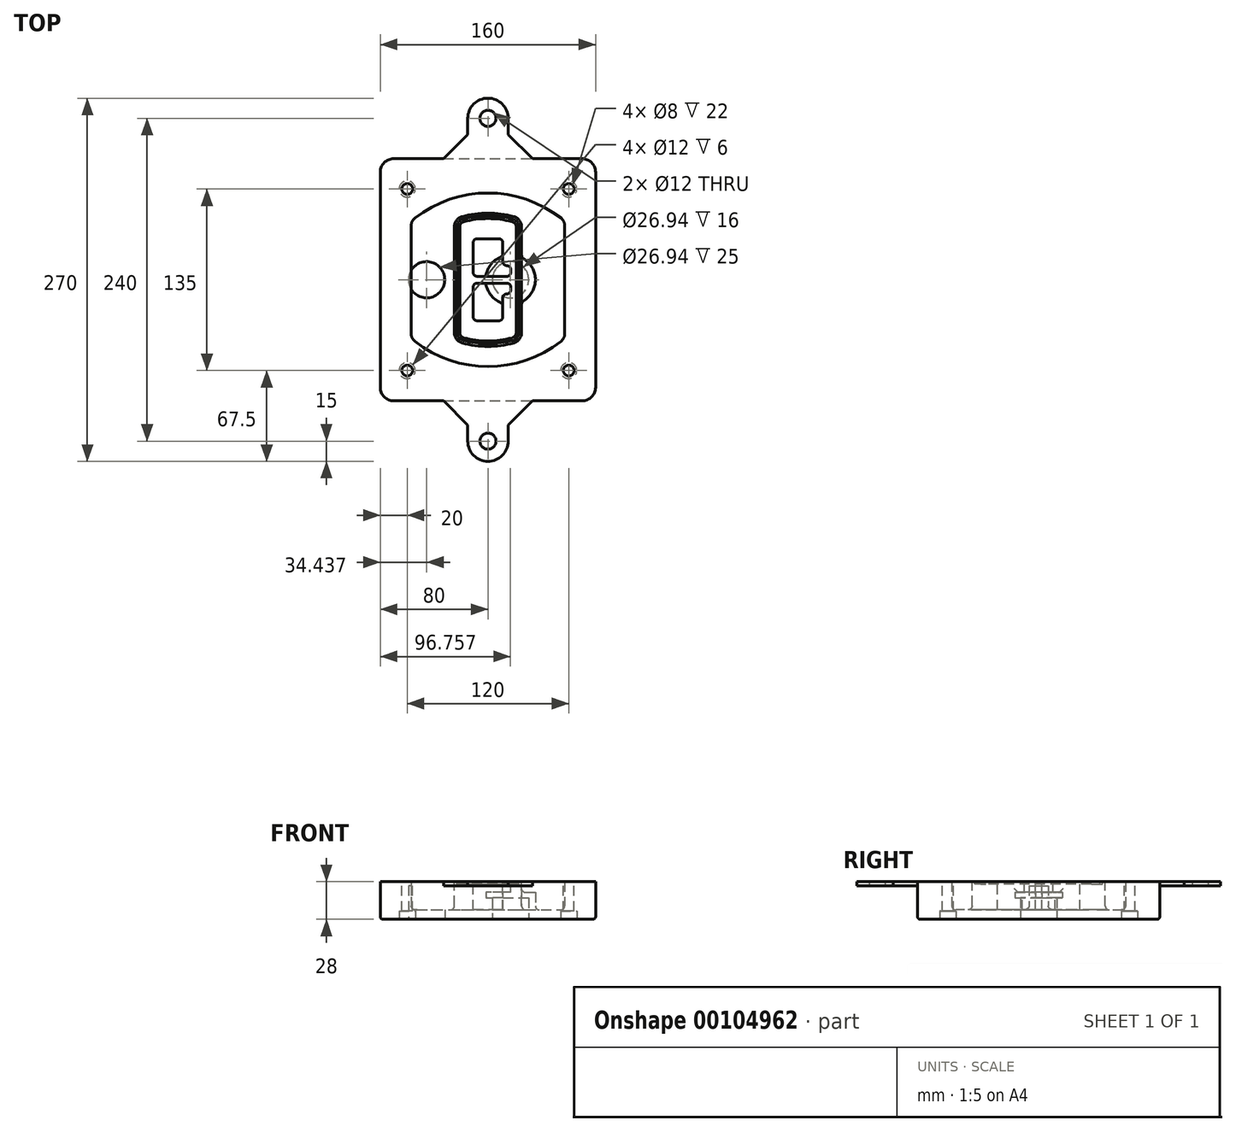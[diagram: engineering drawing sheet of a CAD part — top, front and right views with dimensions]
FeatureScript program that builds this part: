
annotation { "Feature Type Name" : "Feature", "Feature Type Description" : "" }
export const myFeature = defineFeature(function(context is Context, id is Id, definition is map)
    precondition{}
    {
        {
            var Q0;
            Q0=qCreatedBy(makeId("Top.planeOp"),FACE);
            var sketch = newSketch(context, id + "F0", { "sketchPlane" : qUnion([Q0])});
            skPoint(sketch, "E0.rect.middle", {"position": v(0, 0) * mm});
            skLineSegment(sketch, "E1.bottom", {"start": v(-70, -90) * mm, "end": v(70, -90) * mm});
            skLineSegment(sketch, "E1.top", {"start": v(-70, 90) * mm, "end": v(70, 90) * mm});
            skLineSegment(sketch, "E1.left", {"start": v(-80, -80) * mm, "end": v(-80, 80) * mm});
            skLineSegment(sketch, "E1.right", {"start": v(80, -80) * mm, "end": v(80, 80) * mm});
            skLineSegment(sketch, "E2", {"start": v(-80, 90) * mm, "end": v(80, -90) * mm, "construction": true});
            skLineSegment(sketch, "E3", {"start": v(80, 90) * mm, "end": v(-80, -90) * mm, "construction": true});
            skCircle(sketch, "E4", {"center": v(-60, 67.5) * mm, "radius": 4 * mm});
            skCircle(sketch, "E5", {"center": v(60, 67.5) * mm, "radius": 4 * mm});
            skCircle(sketch, "E6", {"center": v(60, -67.5) * mm, "radius": 4 * mm});
            skCircle(sketch, "E7", {"center": v(-60, -67.5) * mm, "radius": 4 * mm});
            skLineSegment(sketch, "E8", {"start": v(-60, 67.5) * mm, "end": v(60, 67.5) * mm, "construction": true});
            skLineSegment(sketch, "E9", {"start": v(60, 67.5) * mm, "end": v(60, -67.5) * mm, "construction": true});
            skLineSegment(sketch, "E10", {"start": v(60, -67.5) * mm, "end": v(-60, -67.5) * mm, "construction": true});
            skLineSegment(sketch, "E11", {"start": v(-60, -67.5) * mm, "end": v(-60, 67.5) * mm, "construction": true});
            skLineSegment(sketch, "E12", {"start": v(-60, 40.3) * mm, "end": v(-60, -40.3) * mm});
            skLineSegment(sketch, "E13", {"start": v(60, 40.3) * mm, "end": v(60, -40.3) * mm});
            skArc(sketch, "E14", {"start": v(56.15, 48.18) * mm, "mid": v(0, 67.5) * mm, "end": v(-56.15, 48.18) * mm});
            skArc(sketch, "E15", {"start": v(-56.15, -48.18) * mm, "mid": v(0, -67.5) * mm, "end": v(56.15, -48.18) * mm});
            skLineSegment(sketch, "E16", {"start": v(-60, 0) * mm, "end": v(60, 0) * mm, "construction": true});
            skPoint(sketch, "E17.visualSharp", {"position": v(-60, -45) * mm});
            skArc(sketch, "E17.filletArc", {"start": v(-60, -40.3) * mm, "mid": v(-58.99, -44.68) * mm, "end": v(-56.15, -48.18) * mm});
            skPoint(sketch, "E18.visualSharp", {"position": v(-60, 45) * mm});
            skArc(sketch, "E18.filletArc", {"start": v(-56.15, 48.18) * mm, "mid": v(-58.99, 44.68) * mm, "end": v(-60, 40.3) * mm});
            skPoint(sketch, "E19.visualSharp", {"position": v(60, 45) * mm});
            skArc(sketch, "E19.filletArc", {"start": v(60, 40.3) * mm, "mid": v(58.99, 44.68) * mm, "end": v(56.15, 48.18) * mm});
            skPoint(sketch, "E20.visualSharp", {"position": v(60, -45) * mm});
            skArc(sketch, "E20.filletArc", {"start": v(56.15, -48.18) * mm, "mid": v(58.99, -44.68) * mm, "end": v(60, -40.3) * mm});
            skPoint(sketch, "E21.visualSharp", {"position": v(-80, 90) * mm});
            skArc(sketch, "E21.filletArc", {"start": v(-70, 90) * mm, "mid": v(-77.07, 87.07) * mm, "end": v(-80, 80) * mm});
            skPoint(sketch, "E22.visualSharp", {"position": v(80, 90) * mm});
            skArc(sketch, "E22.filletArc", {"start": v(80, 80) * mm, "mid": v(77.07, 87.07) * mm, "end": v(70, 90) * mm});
            skPoint(sketch, "E23.visualSharp", {"position": v(80, -90) * mm});
            skArc(sketch, "E23.filletArc", {"start": v(70, -90) * mm, "mid": v(77.07, -87.07) * mm, "end": v(80, -80) * mm});
            skPoint(sketch, "E24.visualSharp", {"position": v(-80, -90) * mm});
            skArc(sketch, "E24.filletArc", {"start": v(-80, -80) * mm, "mid": v(-77.07, -87.07) * mm, "end": v(-70, -90) * mm});
            skArc(sketch, "E25.0", {"start": v(57, 40.3) * mm, "mid": v(56.3, 43.36) * mm, "end": v(54.3, 45.81) * mm});
            skLineSegment(sketch, "E25.1", {"start": v(57, 40.3) * mm, "end": v(57, -40.3) * mm});
            skArc(sketch, "E25.2", {"start": v(54.3, -45.81) * mm, "mid": v(56.3, -43.36) * mm, "end": v(57, -40.3) * mm});
            skArc(sketch, "E25.3", {"start": v(-54.3, -45.81) * mm, "mid": v(0, -64.5) * mm, "end": v(54.3, -45.81) * mm});
            skArc(sketch, "E25.4", {"start": v(-57, -40.3) * mm, "mid": v(-56.3, -43.36) * mm, "end": v(-54.3, -45.81) * mm});
            skArc(sketch, "E25.5", {"start": v(54.3, 45.81) * mm, "mid": v(0, 64.5) * mm, "end": v(-54.3, 45.81) * mm});
            skLineSegment(sketch, "E25.6", {"start": v(-57, 40.3) * mm, "end": v(-57, -40.3) * mm});
            skArc(sketch, "E25.7", {"start": v(-54.3, 45.81) * mm, "mid": v(-56.3, 43.36) * mm, "end": v(-57, 40.3) * mm});
            skArc(sketch, "E26.0", {"start": v(-58.62, 51.33) * mm, "mid": v(-62.58, 46.43) * mm, "end": v(-64, 40.3) * mm});
            skArc(sketch, "E26.1", {"start": v(58.62, 51.33) * mm, "mid": v(0, 71.5) * mm, "end": v(-58.62, 51.33) * mm});
            skArc(sketch, "E26.2", {"start": v(64, 40.3) * mm, "mid": v(62.58, 46.43) * mm, "end": v(58.62, 51.33) * mm});
            skLineSegment(sketch, "E26.3", {"start": v(64, 40.3) * mm, "end": v(64, -40.3) * mm});
            skArc(sketch, "E26.4", {"start": v(58.62, -51.33) * mm, "mid": v(62.58, -46.43) * mm, "end": v(64, -40.3) * mm});
            skLineSegment(sketch, "E26.5", {"start": v(-64, 40.3) * mm, "end": v(-64, -40.3) * mm});
            skArc(sketch, "E26.6", {"start": v(-58.62, -51.33) * mm, "mid": v(0, -71.5) * mm, "end": v(58.62, -51.33) * mm});
            skArc(sketch, "E26.7", {"start": v(-64, -40.3) * mm, "mid": v(-62.58, -46.43) * mm, "end": v(-58.62, -51.33) * mm});
            skSolve(sketch);
        }
        {
            var Q0;
            Q0=makeQuery(id+"F0.imprint","IMPRINT",FACE,{"disambiguationData":[TD([[makeQuery(id+"F0.imprint","IMPRINT",EDGE,{"derivedFrom":sQuery(id+"F0.wireOp",EDGE,"E1.bottom")}),1.0]])]});
            var Q1;
            Q1=makeQuery(id+"F0.imprint","IMPRINT",FACE,{"disambiguationData":[TD([[makeQuery(id+"F0.imprint","IMPRINT",EDGE,{"derivedFrom":sQuery(id+"F0.wireOp",EDGE,"E12")}),1.0]])]});
            var Q2;
            Q2=makeQuery(id+"F0.imprint","IMPRINT",FACE,{"disambiguationData":[TD([[makeQuery(id+"F0.imprint","IMPRINT",EDGE,{"derivedFrom":sQuery(id+"F0.wireOp",EDGE,"E25.0")}),1.0]])]});
            var Q3;
            Q3=makeQuery(id+"F0.imprint","IMPRINT",FACE,{"disambiguationData":[TD([[makeQuery(id+"F0.imprint","IMPRINT",EDGE,{"derivedFrom":sQuery(id+"F0.wireOp",EDGE,"E12")}),-1.0]])]});
            extrude(context, id + "F1", {"entities" : qUnion([Q0, Q1, Q2, Q3]), "oppositeDirection" : true, "depth" : 25 * mm});
        }
        {
            var Q0;
            Q0=makeQuery(id+"F0.imprint","IMPRINT",FACE,{"disambiguationData":[TD([[makeQuery(id+"F0.imprint","IMPRINT",EDGE,{"derivedFrom":sQuery(id+"F0.wireOp",EDGE,"E12")}),1.0]])]});
            extrude(context, id + "F2", {"entities" : qUnion([Q0]), "operationType" : NewBodyOperationType.ADD, "depth" : 3 * mm});
        }
        {
            var Q0;
            Q0=makeQuery(id+"F0.imprint","IMPRINT",FACE,{"disambiguationData":[TD([[makeQuery(id+"F0.imprint","IMPRINT",EDGE,{"derivedFrom":sQuery(id+"F0.wireOp",EDGE,"E25.0")}),1.0]])]});
            extrude(context, id + "F3", {"entities" : qUnion([Q0]), "operationType" : NewBodyOperationType.REMOVE, "oppositeDirection" : true, "depth" : 18 * mm});
        }
        {
            var Q0;
            Q0=makeQuery(id+"F2.opExtrude","CAP_FACE",FACE,{"disambiguationData":[OSD([sQuery(id+"F0.wireOp",EDGE,"E12"),sQuery(id+"F0.wireOp",EDGE,"E13"),sQuery(id+"F0.wireOp",EDGE,"E14"),sQuery(id+"F0.wireOp",EDGE,"E15"),sQuery(id+"F0.wireOp",EDGE,"E17.filletArc"),sQuery(id+"F0.wireOp",EDGE,"E18.filletArc"),sQuery(id+"F0.wireOp",EDGE,"E19.filletArc"),sQuery(id+"F0.wireOp",EDGE,"E20.filletArc"),sQuery(id+"F0.wireOp",EDGE,"E25.0"),sQuery(id+"F0.wireOp",EDGE,"E25.1"),sQuery(id+"F0.wireOp",EDGE,"E25.2"),sQuery(id+"F0.wireOp",EDGE,"E25.3"),sQuery(id+"F0.wireOp",EDGE,"E25.4"),sQuery(id+"F0.wireOp",EDGE,"E25.5"),sQuery(id+"F0.wireOp",EDGE,"E25.6"),sQuery(id+"F0.wireOp",EDGE,"E25.7")])],"isStart":false});
            var sketch = newSketch(context, id + "F4", { "sketchPlane" : qUnion([Q0])});
            skArc(sketch, "E27.0", {"start": v(-19.08, -46.97) * mm, "mid": v(0, -49.5) * mm, "end": v(19.08, -46.97) * mm});
            skArc(sketch, "E28.0", {"start": v(19.08, 46.97) * mm, "mid": v(0, 49.5) * mm, "end": v(-19.08, 46.97) * mm});
            skLineSegment(sketch, "E29", {"start": v(-25, 39.25) * mm, "end": v(-25, -39.25) * mm});
            skLineSegment(sketch, "E30", {"start": v(25, 39.25) * mm, "end": v(25, -39.25) * mm});
            skLineSegment(sketch, "E31", {"start": v(-25, 45.1) * mm, "end": v(25, 45.1) * mm, "construction": true});
            skLineSegment(sketch, "E32", {"start": v(-25, -45.1) * mm, "end": v(25, -45.1) * mm, "construction": true});
            skPoint(sketch, "E33.visualSharp", {"position": v(-25, 45.1) * mm});
            skArc(sketch, "E33.filletArc", {"start": v(-19.08, 46.97) * mm, "mid": v(-23.35, 44.11) * mm, "end": v(-25, 39.25) * mm});
            skPoint(sketch, "E34.visualSharp", {"position": v(25, 45.1) * mm});
            skArc(sketch, "E34.filletArc", {"start": v(25, 39.25) * mm, "mid": v(23.35, 44.11) * mm, "end": v(19.08, 46.97) * mm});
            skPoint(sketch, "E35.visualSharp", {"position": v(25, -45.1) * mm});
            skArc(sketch, "E35.filletArc", {"start": v(19.08, -46.97) * mm, "mid": v(23.35, -44.11) * mm, "end": v(25, -39.25) * mm});
            skPoint(sketch, "E36.visualSharp", {"position": v(-25, -45.1) * mm});
            skArc(sketch, "E36.filletArc", {"start": v(-25, -39.25) * mm, "mid": v(-23.35, -44.11) * mm, "end": v(-19.08, -46.97) * mm});
            skArc(sketch, "E37.0", {"start": v(54.3, 45.81) * mm, "mid": v(0, 64.5) * mm, "end": v(-54.3, 45.81) * mm});
            skArc(sketch, "E37.1", {"start": v(-54.3, 45.81) * mm, "mid": v(-56.3, 43.36) * mm, "end": v(-57, 40.3) * mm});
            skLineSegment(sketch, "E37.2", {"start": v(-57, 40.3) * mm, "end": v(-57, -40.3) * mm});
            skArc(sketch, "E37.3", {"start": v(-57, -40.3) * mm, "mid": v(-56.3, -43.36) * mm, "end": v(-54.3, -45.81) * mm});
            skArc(sketch, "E37.4", {"start": v(-54.3, -45.81) * mm, "mid": v(0, -64.5) * mm, "end": v(54.3, -45.81) * mm});
            skArc(sketch, "E37.5", {"start": v(54.3, -45.81) * mm, "mid": v(56.3, -43.36) * mm, "end": v(57, -40.3) * mm});
            skLineSegment(sketch, "E37.6", {"start": v(57, 40.3) * mm, "end": v(57, -40.3) * mm});
            skArc(sketch, "E37.7", {"start": v(57, 40.3) * mm, "mid": v(56.3, 43.36) * mm, "end": v(54.3, 45.81) * mm});
            skLineSegment(sketch, "E38.0", {"start": v(23, 39.25) * mm, "end": v(23, -39.25) * mm});
            skArc(sketch, "E38.1", {"start": v(18.56, -45.04) * mm, "mid": v(21.76, -42.9) * mm, "end": v(23, -39.25) * mm});
            skArc(sketch, "E38.2", {"start": v(-18.56, -45.04) * mm, "mid": v(0, -47.5) * mm, "end": v(18.56, -45.04) * mm});
            skArc(sketch, "E38.3", {"start": v(-23, -39.25) * mm, "mid": v(-21.76, -42.9) * mm, "end": v(-18.56, -45.04) * mm});
            skLineSegment(sketch, "E38.4", {"start": v(-23, 39.25) * mm, "end": v(-23, -39.25) * mm});
            skArc(sketch, "E38.5", {"start": v(23, 39.25) * mm, "mid": v(21.76, 42.9) * mm, "end": v(18.56, 45.04) * mm});
            skArc(sketch, "E38.6", {"start": v(-18.56, 45.04) * mm, "mid": v(-21.76, 42.9) * mm, "end": v(-23, 39.25) * mm});
            skArc(sketch, "E38.7", {"start": v(18.56, 45.04) * mm, "mid": v(0, 47.5) * mm, "end": v(-18.56, 45.04) * mm});
            skArc(sketch, "E39.0", {"start": v(21, 39.25) * mm, "mid": v(20.18, 41.68) * mm, "end": v(18.04, 43.1) * mm});
            skLineSegment(sketch, "E39.1", {"start": v(21, 39.25) * mm, "end": v(21, -39.25) * mm});
            skArc(sketch, "E39.2", {"start": v(18.04, -43.1) * mm, "mid": v(20.18, -41.68) * mm, "end": v(21, -39.25) * mm});
            skArc(sketch, "E39.3", {"start": v(-18.04, -43.1) * mm, "mid": v(0, -45.5) * mm, "end": v(18.04, -43.1) * mm});
            skArc(sketch, "E39.4", {"start": v(-21, -39.25) * mm, "mid": v(-20.18, -41.68) * mm, "end": v(-18.04, -43.1) * mm});
            skArc(sketch, "E39.5", {"start": v(18.04, 43.1) * mm, "mid": v(0, 45.5) * mm, "end": v(-18.04, 43.1) * mm});
            skLineSegment(sketch, "E39.6", {"start": v(-21, 39.25) * mm, "end": v(-21, -39.25) * mm});
            skArc(sketch, "E39.7", {"start": v(-18.04, 43.1) * mm, "mid": v(-20.18, 41.68) * mm, "end": v(-21, 39.25) * mm});
            skLineSegment(sketch, "E40", {"start": v(-25, 0) * mm, "end": v(25, 0) * mm, "construction": true});
            skLineSegment(sketch, "E41", {"start": v(-11, 5.5) * mm, "end": v(-11, 27.5) * mm});
            skLineSegment(sketch, "E42", {"start": v(-8, 30.5) * mm, "end": v(8, 30.5) * mm});
            skLineSegment(sketch, "E43", {"start": v(11, 27.5) * mm, "end": v(11, 13.5) * mm});
            skLineSegment(sketch, "E44", {"start": v(14, 10.5) * mm, "end": v(14, 10.5) * mm});
            skLineSegment(sketch, "E45", {"start": v(17, 7.5) * mm, "end": v(17, 5.5) * mm});
            skLineSegment(sketch, "E46", {"start": v(14, 2.5) * mm, "end": v(-8, 2.5) * mm});
            skPoint(sketch, "E47.visualSharp", {"position": v(-11, 30.5) * mm});
            skArc(sketch, "E47.filletArc", {"start": v(-8, 30.5) * mm, "mid": v(-10.12, 29.62) * mm, "end": v(-11, 27.5) * mm});
            skPoint(sketch, "E48.visualSharp", {"position": v(11, 30.5) * mm});
            skArc(sketch, "E48.filletArc", {"start": v(11, 27.5) * mm, "mid": v(10.12, 29.62) * mm, "end": v(8, 30.5) * mm});
            skPoint(sketch, "E49.visualSharp", {"position": v(11, 10.5) * mm});
            skArc(sketch, "E49.filletArc", {"start": v(11, 13.5) * mm, "mid": v(11.88, 11.38) * mm, "end": v(14, 10.5) * mm});
            skPoint(sketch, "E50.visualSharp", {"position": v(17, 10.5) * mm});
            skArc(sketch, "E50.filletArc", {"start": v(17, 7.5) * mm, "mid": v(16.12, 9.62) * mm, "end": v(14, 10.5) * mm});
            skPoint(sketch, "E51.visualSharp", {"position": v(17, 2.5) * mm});
            skArc(sketch, "E51.filletArc", {"start": v(14, 2.5) * mm, "mid": v(16.12, 3.38) * mm, "end": v(17, 5.5) * mm});
            skPoint(sketch, "E52.visualSharp", {"position": v(-11, 2.5) * mm});
            skArc(sketch, "E52.filletArc", {"start": v(-11, 5.5) * mm, "mid": v(-10.12, 3.38) * mm, "end": v(-8, 2.5) * mm});
            skLineSegment(sketch, "E53.0.MirrorCS", {"start": v(14, -2.5) * mm, "end": v(-8, -2.5) * mm});
            skArc(sketch, "E54.0.MirrorCS", {"start": v(-11, -5.5) * mm, "mid": v(-10.12, -3.38) * mm, "end": v(-8, -2.5) * mm});
            skLineSegment(sketch, "E55.0.MirrorCS", {"start": v(-11, -5.5) * mm, "end": v(-11, -27.5) * mm});
            skArc(sketch, "E56.0.MirrorCS", {"start": v(-8, -30.5) * mm, "mid": v(-10.12, -29.62) * mm, "end": v(-11, -27.5) * mm});
            skLineSegment(sketch, "E57.0.MirrorCS", {"start": v(-8, -30.5) * mm, "end": v(8, -30.5) * mm});
            skArc(sketch, "E58.0.MirrorCS", {"start": v(11, -27.5) * mm, "mid": v(10.12, -29.62) * mm, "end": v(8, -30.5) * mm});
            skLineSegment(sketch, "E59.0.MirrorCS", {"start": v(11, -27.5) * mm, "end": v(11, -13.5) * mm});
            skArc(sketch, "E60.0.MirrorCS", {"start": v(11, -13.5) * mm, "mid": v(11.88, -11.38) * mm, "end": v(14, -10.5) * mm});
            skArc(sketch, "E61.0.MirrorCS", {"start": v(17, -7.5) * mm, "mid": v(16.12, -9.62) * mm, "end": v(14, -10.5) * mm});
            skLineSegment(sketch, "E62.0.MirrorCS", {"start": v(17, -7.5) * mm, "end": v(17, -5.5) * mm});
            skArc(sketch, "E63.0.MirrorCS", {"start": v(14, -2.5) * mm, "mid": v(16.12, -3.38) * mm, "end": v(17, -5.5) * mm});
            skSolve(sketch);
        }
        {
            var Q0;
            Q0=makeQuery(id+"F4.imprint","IMPRINT",FACE,{"disambiguationData":[TD([[makeQuery(id+"F4.imprint","IMPRINT",EDGE,{"derivedFrom":sQuery(id+"F4.wireOp",EDGE,"E27.0")}),1.0]])]});
            var Q1;
            Q1=makeQuery(id+"F4.imprint","IMPRINT",FACE,{"disambiguationData":[TD([[makeQuery(id+"F4.imprint","IMPRINT",EDGE,{"derivedFrom":sQuery(id+"F4.wireOp",EDGE,"E38.0")}),-1.0]])]});
            var Q2;
            Q2=makeQuery(id+"F4.imprint","IMPRINT",FACE,{"disambiguationData":[TD([[makeQuery(id+"F4.imprint","IMPRINT",EDGE,{"derivedFrom":sQuery(id+"F4.wireOp",EDGE,"E39.0")}),1.0]])]});
            extrude(context, id + "F5", {"entities" : qUnion([Q0, Q1, Q2]), "operationType" : NewBodyOperationType.ADD, "endBound" : BoundingType.UP_TO_NEXT, "oppositeDirection" : true, "depth" : 25 * mm});
        }
        {
            var Q0;
            Q0=makeQuery(id+"F4.imprint","IMPRINT",FACE,{"disambiguationData":[TD([[makeQuery(id+"F4.imprint","IMPRINT",EDGE,{"derivedFrom":sQuery(id+"F4.wireOp",EDGE,"E38.0")}),-1.0]])]});
            extrude(context, id + "F6", {"entities" : qUnion([Q0]), "operationType" : NewBodyOperationType.REMOVE, "oppositeDirection" : true, "depth" : 2 * mm});
        }
        {
            var Q0;
            Q0=makeQuery(id+"F1.opExtrude","CAP_FACE",FACE,{"disambiguationData":[OSD([sQuery(id+"F0.wireOp",EDGE,"E1.bottom"),sQuery(id+"F0.wireOp",EDGE,"E1.top"),sQuery(id+"F0.wireOp",EDGE,"E1.left"),sQuery(id+"F0.wireOp",EDGE,"E1.right"),sQuery(id+"F0.wireOp",EDGE,"E4"),sQuery(id+"F0.wireOp",EDGE,"E5"),sQuery(id+"F0.wireOp",EDGE,"E6"),sQuery(id+"F0.wireOp",EDGE,"E7"),sQuery(id+"F0.wireOp",EDGE,"E21.filletArc"),sQuery(id+"F0.wireOp",EDGE,"E22.filletArc"),sQuery(id+"F0.wireOp",EDGE,"E23.filletArc"),sQuery(id+"F0.wireOp",EDGE,"E24.filletArc")])],"isStart":false});
            var sketch = newSketch(context, id + "F7", { "sketchPlane" : qUnion([Q0])});
            skCircle(sketch, "E64", {"center": v(16.76, 0) * mm, "radius": 13.47 * mm});
            skCircle(sketch, "E65", {"center": v(-45.56, 0) * mm, "radius": 13.47 * mm});
            skLineSegment(sketch, "E66", {"start": v(80, 0) * mm, "end": v(-80, 0) * mm});
            skCircle(sketch, "E67", {"center": v(16.76, 0) * mm, "radius": 18.47 * mm});
            skCircle(sketch, "E68", {"center": v(60, -67.5) * mm, "radius": 6 * mm});
            skCircle(sketch, "E69", {"center": v(-60, -67.5) * mm, "radius": 6 * mm});
            skCircle(sketch, "E70", {"center": v(-60, 67.5) * mm, "radius": 6 * mm});
            skCircle(sketch, "E71", {"center": v(60, 67.5) * mm, "radius": 6 * mm});
            skSolve(sketch);
        }
        {
            var Q0;
            {var subQ1=sQuery(id+"F7.wireOp",EDGE,"E66");var subQ4=sQuery(id+"F7.wireOp",EDGE,"E64");var subQ6=makeQuery(id+"F7.imprint","INTERSECT",VERTEX,{"disambiguationData":[OD(0.0)],"derivedFrom":[subQ4,subQ1]});Q0=makeQuery(id+"F7.imprint","IMPRINT",FACE,{"disambiguationData":[TD([[makeQuery(id+"F7.imprint","IMPRINT",EDGE,{"disambiguationData":[TD([[subQ6,-1.0]])],"derivedFrom":subQ4}),-1.0]])]});}
            var Q1;
            {var subQ0=sQuery(id+"F7.wireOp",EDGE,"E66");var subQ1=sQuery(id+"F7.wireOp",EDGE,"E64");var subQ3=makeQuery(id+"F7.imprint","INTERSECT",VERTEX,{"disambiguationData":[OD(0.0)],"derivedFrom":[subQ1,subQ0]});Q1=makeQuery(id+"F7.imprint","IMPRINT",FACE,{"disambiguationData":[TD([[makeQuery(id+"F7.imprint","IMPRINT",EDGE,{"disambiguationData":[TD([[subQ3,-1.0]])],"derivedFrom":subQ1}),1.0]])]});}
            var Q2;
            {var subQ0=sQuery(id+"F7.wireOp",EDGE,"E66");var subQ1=sQuery(id+"F7.wireOp",EDGE,"E64");var subQ3=makeQuery(id+"F7.imprint","INTERSECT",VERTEX,{"disambiguationData":[OD(0.0)],"derivedFrom":[subQ1,subQ0]});Q2=makeQuery(id+"F7.imprint","IMPRINT",FACE,{"disambiguationData":[TD([[makeQuery(id+"F7.imprint","IMPRINT",EDGE,{"disambiguationData":[TD([[subQ3,1.0]])],"derivedFrom":subQ1}),1.0]])]});}
            var Q3;
            {var subQ1=sQuery(id+"F7.wireOp",EDGE,"E66");var subQ4=sQuery(id+"F7.wireOp",EDGE,"E64");var subQ6=makeQuery(id+"F7.imprint","INTERSECT",VERTEX,{"disambiguationData":[OD(0.0)],"derivedFrom":[subQ4,subQ1]});Q3=makeQuery(id+"F7.imprint","IMPRINT",FACE,{"disambiguationData":[TD([[makeQuery(id+"F7.imprint","IMPRINT",EDGE,{"disambiguationData":[TD([[subQ6,1.0]])],"derivedFrom":subQ4}),-1.0]])]});}
            extrude(context, id + "F8", {"entities" : qUnion([Q0, Q1, Q2, Q3]), "operationType" : NewBodyOperationType.ADD, "oppositeDirection" : true, "depth" : 20 * mm});
        }
        {
            var Q0;
            {var subQ0=sQuery(id+"F7.wireOp",EDGE,"E66");var subQ1=sQuery(id+"F7.wireOp",EDGE,"E64");var subQ3=makeQuery(id+"F7.imprint","INTERSECT",VERTEX,{"disambiguationData":[OD(0.0)],"derivedFrom":[subQ1,subQ0]});Q0=makeQuery(id+"F7.imprint","IMPRINT",FACE,{"disambiguationData":[TD([[makeQuery(id+"F7.imprint","IMPRINT",EDGE,{"disambiguationData":[TD([[subQ3,-1.0]])],"derivedFrom":subQ1}),1.0]])]});}
            var Q1;
            {var subQ0=sQuery(id+"F7.wireOp",EDGE,"E66");var subQ1=sQuery(id+"F7.wireOp",EDGE,"E64");var subQ3=makeQuery(id+"F7.imprint","INTERSECT",VERTEX,{"disambiguationData":[OD(0.0)],"derivedFrom":[subQ1,subQ0]});Q1=makeQuery(id+"F7.imprint","IMPRINT",FACE,{"disambiguationData":[TD([[makeQuery(id+"F7.imprint","IMPRINT",EDGE,{"disambiguationData":[TD([[subQ3,1.0]])],"derivedFrom":subQ1}),1.0]])]});}
            extrude(context, id + "F9", {"entities" : qUnion([Q0, Q1]), "operationType" : NewBodyOperationType.REMOVE, "oppositeDirection" : true, "depth" : 16 * mm});
        }
        {
            var Q0;
            {var subQ0=sQuery(id+"F7.wireOp",EDGE,"E66");var subQ1=sQuery(id+"F7.wireOp",EDGE,"E65");var subQ3=makeQuery(id+"F7.imprint","INTERSECT",VERTEX,{"disambiguationData":[OD(0.0)],"derivedFrom":[subQ1,subQ0]});Q0=makeQuery(id+"F7.imprint","IMPRINT",FACE,{"disambiguationData":[TD([[makeQuery(id+"F7.imprint","IMPRINT",EDGE,{"disambiguationData":[TD([[subQ3,-1.0]])],"derivedFrom":subQ1}),1.0]])]});}
            var Q1;
            {var subQ0=sQuery(id+"F7.wireOp",EDGE,"E66");var subQ1=sQuery(id+"F7.wireOp",EDGE,"E65");var subQ3=makeQuery(id+"F7.imprint","INTERSECT",VERTEX,{"disambiguationData":[OD(0.0)],"derivedFrom":[subQ1,subQ0]});Q1=makeQuery(id+"F7.imprint","IMPRINT",FACE,{"disambiguationData":[TD([[makeQuery(id+"F7.imprint","IMPRINT",EDGE,{"disambiguationData":[TD([[subQ3,1.0]])],"derivedFrom":subQ1}),1.0]])]});}
            extrude(context, id + "F10", {"entities" : qUnion([Q0, Q1]), "operationType" : NewBodyOperationType.REMOVE, "oppositeDirection" : true, "depth" : 25 * mm});
        }
        {
            var Q0;
            Q0=makeQuery(id+"F7.imprint","IMPRINT",FACE,{"disambiguationData":[TD([[makeQuery(id+"F7.imprint","IMPRINT",EDGE,{"derivedFrom":sQuery(id+"F7.wireOp",EDGE,"E68")}),1.0]])]});
            var Q1;
            Q1=makeQuery(id+"F7.imprint","IMPRINT",FACE,{"disambiguationData":[TD([[makeQuery(id+"F7.imprint","IMPRINT",EDGE,{"derivedFrom":makeQuery(id+"F1.opExtrude","CAP_EDGE",EDGE,{"disambiguationData":[OSD([sQuery(id+"F0.wireOp",EDGE,"E5")])],"isStart":false})}),-1.0]])]});
            var Q2;
            Q2=makeQuery(id+"F7.imprint","IMPRINT",FACE,{"disambiguationData":[TD([[makeQuery(id+"F7.imprint","IMPRINT",EDGE,{"derivedFrom":sQuery(id+"F7.wireOp",EDGE,"E69")}),1.0]])]});
            var Q3;
            Q3=makeQuery(id+"F7.imprint","IMPRINT",FACE,{"disambiguationData":[TD([[makeQuery(id+"F7.imprint","IMPRINT",EDGE,{"derivedFrom":makeQuery(id+"F1.opExtrude","CAP_EDGE",EDGE,{"disambiguationData":[OSD([sQuery(id+"F0.wireOp",EDGE,"E4")])],"isStart":false})}),-1.0]])]});
            var Q4;
            Q4=makeQuery(id+"F7.imprint","IMPRINT",FACE,{"disambiguationData":[TD([[makeQuery(id+"F7.imprint","IMPRINT",EDGE,{"derivedFrom":sQuery(id+"F7.wireOp",EDGE,"E70")}),1.0]])]});
            var Q5;
            Q5=makeQuery(id+"F7.imprint","IMPRINT",FACE,{"disambiguationData":[TD([[makeQuery(id+"F7.imprint","IMPRINT",EDGE,{"derivedFrom":makeQuery(id+"F1.opExtrude","CAP_EDGE",EDGE,{"disambiguationData":[OSD([sQuery(id+"F0.wireOp",EDGE,"E7")])],"isStart":false})}),-1.0]])]});
            var Q6;
            Q6=makeQuery(id+"F7.imprint","IMPRINT",FACE,{"disambiguationData":[TD([[makeQuery(id+"F7.imprint","IMPRINT",EDGE,{"derivedFrom":sQuery(id+"F7.wireOp",EDGE,"E71")}),1.0]])]});
            var Q7;
            Q7=makeQuery(id+"F7.imprint","IMPRINT",FACE,{"disambiguationData":[TD([[makeQuery(id+"F7.imprint","IMPRINT",EDGE,{"derivedFrom":makeQuery(id+"F1.opExtrude","CAP_EDGE",EDGE,{"disambiguationData":[OSD([sQuery(id+"F0.wireOp",EDGE,"E6")])],"isStart":false})}),-1.0]])]});
            extrude(context, id + "F11", {"entities" : qUnion([Q0, Q1, Q2, Q3, Q4, Q5, Q6, Q7]), "operationType" : NewBodyOperationType.REMOVE, "oppositeDirection" : true, "depth" : 6 * mm});
        }
        {
            var Q0;
            Q0=makeQuery(id+"F9.boolean.opBoolean","COPY",FACE,{"derivedFrom":makeQuery(id+"F9.opExtrude","CAP_FACE",FACE,{"disambiguationData":[OSD([sQuery(id+"F7.wireOp",EDGE,"E64")])],"isStart":false})});
            var sketch = newSketch(context, id + "F12", { "sketchPlane" : qUnion([Q0])});
            skArc(sketch, "E72.0", {"start": v(11, 17.55) * mm, "mid": v(2.57, 11.82) * mm, "end": v(-1.54, 2.5) * mm});
            skArc(sketch, "E72.1", {"start": v(-1.54, -2.5) * mm, "mid": v(2.57, -11.82) * mm, "end": v(11, -17.55) * mm});
            skLineSegment(sketch, "E73", {"start": v(-1.54, -2.5) * mm, "end": v(14, -2.5) * mm});
            skLineSegment(sketch, "E74.0", {"start": v(14, 2.5) * mm, "end": v(-1.54, 2.5) * mm});
            skArc(sketch, "E74.1", {"start": v(14, 2.5) * mm, "mid": v(16.12, 3.38) * mm, "end": v(17, 5.5) * mm});
            skLineSegment(sketch, "E74.2", {"start": v(17, 7.5) * mm, "end": v(17, 5.5) * mm});
            skArc(sketch, "E74.3", {"start": v(17, 7.5) * mm, "mid": v(16.12, 9.62) * mm, "end": v(14, 10.5) * mm});
            skArc(sketch, "E74.4", {"start": v(11, 13.5) * mm, "mid": v(11.88, 11.38) * mm, "end": v(14, 10.5) * mm});
            skLineSegment(sketch, "E74.5", {"start": v(11, 17.55) * mm, "end": v(11, 13.5) * mm});
            skLineSegment(sketch, "E74.7", {"start": v(14, -2.5) * mm, "end": v(-1.54, -2.5) * mm});
            skArc(sketch, "E74.8", {"start": v(14, -2.5) * mm, "mid": v(16.12, -3.38) * mm, "end": v(17, -5.5) * mm});
            skLineSegment(sketch, "E74.9", {"start": v(17, -7.5) * mm, "end": v(17, -5.5) * mm});
            skArc(sketch, "E74.10", {"start": v(17, -7.5) * mm, "mid": v(16.12, -9.62) * mm, "end": v(14, -10.5) * mm});
            skArc(sketch, "E74.11", {"start": v(11, -13.5) * mm, "mid": v(11.88, -11.38) * mm, "end": v(14, -10.5) * mm});
            skLineSegment(sketch, "E74.12", {"start": v(11, -17.55) * mm, "end": v(11, -13.5) * mm});
            skPoint(sketch, "E75.orphan", {"position": v(11, -27.5) * mm});
            skPoint(sketch, "E76.orphan", {"position": v(-8, -2.5) * mm});
            skPoint(sketch, "E77.orphan", {"position": v(-8, 2.5) * mm});
            skPoint(sketch, "E78.orphan", {"position": v(11, 27.5) * mm});
            skSolve(sketch);
        }
        {
            var Q0;
            {var subQ7=sQuery(id+"F12.wireOp",EDGE,"E72.0");var subQ14=sQuery(id+"F12.wireOp",EDGE,"E72.1");var subQ16=sQuery(id+"F12.wireOp",EDGE,"E74.1");var subQ18=sQuery(id+"F12.wireOp",EDGE,"E74.8");Q0=qUnion([makeQuery(id+"F12.imprint","IMPRINT",FACE,{"disambiguationData":[TD([[makeQuery(id+"F12.imprint","IMPRINT",EDGE,{"derivedFrom":subQ7}),1.0]])]}),makeQuery(id+"F12.imprint","IMPRINT",FACE,{"disambiguationData":[TD([[makeQuery(id+"F12.imprint","IMPRINT",EDGE,{"derivedFrom":subQ14}),1.0]])]}),makeQuery(id+"F12.imprint","IMPRINT",FACE,{"disambiguationData":[TD([[makeQuery(id+"F12.imprint","IMPRINT",EDGE,{"derivedFrom":subQ16}),1.0]])]}),makeQuery(id+"F12.imprint","IMPRINT",FACE,{"disambiguationData":[TD([[makeQuery(id+"F12.imprint","IMPRINT",EDGE,{"derivedFrom":subQ18}),-1.0]])]})]);}
            var Q1;
            Q1=makeQuery(id+"F5.boolean.opBoolean","SPLIT",FACE,{"disambiguationData":[TD([makeQuery(id+"F5.opExtrude","SWEPT_FACE",FACE,{"disambiguationData":[OSD([sQuery(id+"F4.wireOp",EDGE,"E41")])]})])],"derivedFrom":makeQuery(id+"F3.boolean.opBoolean","COPY",FACE,{"derivedFrom":makeQuery(id+"F3.opExtrude","CAP_FACE",FACE,{"disambiguationData":[OSD([sQuery(id+"F0.wireOp",EDGE,"E25.0"),sQuery(id+"F0.wireOp",EDGE,"E25.1"),sQuery(id+"F0.wireOp",EDGE,"E25.2"),sQuery(id+"F0.wireOp",EDGE,"E25.3"),sQuery(id+"F0.wireOp",EDGE,"E25.4"),sQuery(id+"F0.wireOp",EDGE,"E25.5"),sQuery(id+"F0.wireOp",EDGE,"E25.6"),sQuery(id+"F0.wireOp",EDGE,"E25.7")])],"isStart":false})})});
            extrude(context, id + "F13", {"entities" : qUnion([Q0]), "operationType" : NewBodyOperationType.REMOVE, "endBound" : BoundingType.UP_TO_SURFACE, "endBoundEntityFace" : qUnion([Q1]), "depth" : 25 * mm});
        }
        {
            var Q0;
            Q0=makeQuery(id+"F3.boolean.opBoolean","COPY",EDGE,{"derivedFrom":makeQuery(id+"F3.opExtrude","CAP_EDGE",EDGE,{"disambiguationData":[OSD([sQuery(id+"F0.wireOp",EDGE,"E25.6")])],"isStart":false})});
            var Q1;
            Q1=makeQuery(id+"F8.boolean.opBoolean","INTERSECT",EDGE,{"derivedFrom":[makeQuery(id+"F5.opExtrude","SWEPT_FACE",FACE,{"disambiguationData":[OSD([sQuery(id+"F4.wireOp",EDGE,"E30")])]}),makeQuery(id+"F8.opExtrude","CAP_FACE",FACE,{"disambiguationData":[OSD([sQuery(id+"F7.wireOp",EDGE,"E67")])],"isStart":false})]});
            var Q2;
            Q2=makeQuery(id+"F8.boolean.opBoolean","INTERSECT",EDGE,{"disambiguationData":[OD(1.0)],"derivedFrom":[makeQuery(id+"F5.opExtrude","SWEPT_FACE",FACE,{"disambiguationData":[OSD([sQuery(id+"F4.wireOp",EDGE,"E30")])]}),makeQuery(id+"F8.opExtrude","SWEPT_FACE",FACE,{"disambiguationData":[OSD([sQuery(id+"F7.wireOp",EDGE,"E67")])]})]});
            var Q3;
            {var subQ0=sQuery(id+"F4.wireOp",EDGE,"E30");Q3=makeQuery(id+"F8.boolean.opBoolean","SPLIT",EDGE,{"disambiguationData":[TD([makeQuery(id+"F5.opExtrude","SWEPT_FACE",FACE,{"disambiguationData":[OSD([sQuery(id+"F4.wireOp",EDGE,"E35.filletArc")])]})])],"derivedFrom":makeQuery(id+"F5.opExtrude","CAP_EDGE",EDGE,{"disambiguationData":[OSD([subQ0])],"isStart":false})});}
            var Q4;
            {var subQ0=sQuery(id+"F0.wireOp",EDGE,"E25.7");var subQ1=sQuery(id+"F0.wireOp",EDGE,"E25.1");var subQ2=sQuery(id+"F0.wireOp",EDGE,"E25.6");var subQ3=sQuery(id+"F0.wireOp",EDGE,"E25.5");var subQ4=sQuery(id+"F0.wireOp",EDGE,"E25.4");var subQ5=sQuery(id+"F0.wireOp",EDGE,"E25.0");var subQ6=sQuery(id+"F0.wireOp",EDGE,"E25.2");var subQ7=sQuery(id+"F0.wireOp",EDGE,"E25.3");Q4=makeQuery(id+"F8.boolean.opBoolean","INTERSECT",EDGE,{"derivedFrom":[makeQuery(id+"F5.boolean.opBoolean","SPLIT",FACE,{"disambiguationData":[TD([makeQuery(id+"F2.opExtrude","SWEPT_FACE",FACE,{"disambiguationData":[OSD([subQ5])]})])],"derivedFrom":makeQuery(id+"F3.boolean.opBoolean","COPY",FACE,{"derivedFrom":makeQuery(id+"F3.opExtrude","CAP_FACE",FACE,{"disambiguationData":[OSD([subQ5,subQ1,subQ6,subQ7,subQ4,subQ3,subQ2,subQ0])],"isStart":false})})}),makeQuery(id+"F8.opExtrude","SWEPT_FACE",FACE,{"disambiguationData":[OSD([sQuery(id+"F7.wireOp",EDGE,"E67")])]})]});}
            var Q5;
            Q5=makeQuery(id+"F8.boolean.opBoolean","INTERSECT",EDGE,{"disambiguationData":[OD(0.0)],"derivedFrom":[makeQuery(id+"F5.opExtrude","SWEPT_FACE",FACE,{"disambiguationData":[OSD([sQuery(id+"F4.wireOp",EDGE,"E30")])]}),makeQuery(id+"F8.opExtrude","SWEPT_FACE",FACE,{"disambiguationData":[OSD([sQuery(id+"F7.wireOp",EDGE,"E67")])]})]});
            fillet(context, id + "F14", {"entities" : qUnion([Q0, Q1, Q2, Q3, Q4, Q5]), "radius" : 3 * mm, "tangentPropagation" : true, "allowEdgeOverflow" : false});
        }
        {
            var Q0;
            Q0=makeQuery(id+"F1.opExtrude","CAP_EDGE",EDGE,{"disambiguationData":[OSD([sQuery(id+"F0.wireOp",EDGE,"E1.bottom")])],"isStart":false});
            fillet(context, id + "F15", {"entities" : qUnion([Q0]), "radius" : 2 * mm, "tangentPropagation" : true, "allowEdgeOverflow" : false});
        }
        {
            var Q0;
            {var subQ0=sQuery(id+"F0.wireOp",EDGE,"E22.filletArc");var subQ1=sQuery(id+"F0.wireOp",EDGE,"E7");var subQ2=sQuery(id+"F0.wireOp",EDGE,"E6");var subQ3=sQuery(id+"F0.wireOp",EDGE,"E5");var subQ4=sQuery(id+"F0.wireOp",EDGE,"E4");var subQ5=sQuery(id+"F0.wireOp",EDGE,"E1.bottom");var subQ6=sQuery(id+"F0.wireOp",EDGE,"E21.filletArc");var subQ7=sQuery(id+"F0.wireOp",EDGE,"E1.top");var subQ8=sQuery(id+"F0.wireOp",EDGE,"E1.left");var subQ9=sQuery(id+"F0.wireOp",EDGE,"E1.right");var subQ10=sQuery(id+"F0.wireOp",EDGE,"E23.filletArc");var subQ11=sQuery(id+"F0.wireOp",EDGE,"E24.filletArc");Q0=makeQuery(id+"F2.boolean.opBoolean","SPLIT",FACE,{"disambiguationData":[TD([makeQuery(id+"F1.opExtrude","SWEPT_FACE",FACE,{"disambiguationData":[OSD([subQ5])]})])],"derivedFrom":makeQuery(id+"F1.opExtrude","CAP_FACE",FACE,{"disambiguationData":[OSD([subQ5,subQ7,subQ8,subQ9,subQ4,subQ3,subQ2,subQ1,subQ6,subQ0,subQ10,subQ11])],"isStart":true})});}
            var sketch = newSketch(context, id + "F16", { "sketchPlane" : qUnion([Q0])});
            skLineSegment(sketch, "E79", {"start": v(0, 90) * mm, "end": v(0, 120) * mm, "construction": true});
            skCircle(sketch, "E80", {"center": v(0, 120) * mm, "radius": 6 * mm});
            skLineSegment(sketch, "E81", {"start": v(-15, 120) * mm, "end": v(-15, 120) * mm});
            skLineSegment(sketch, "E82", {"start": v(15, 120) * mm, "end": v(15, 120) * mm});
            skArc(sketch, "E83", {"start": v(15, 120) * mm, "mid": v(0, 135) * mm, "end": v(-15, 120) * mm});
            skLineSegment(sketch, "E84", {"start": v(-33, 90) * mm, "end": v(-15, 108) * mm});
            skLineSegment(sketch, "E85", {"start": v(-15, 108) * mm, "end": v(-15, 120) * mm});
            skLineSegment(sketch, "E86", {"start": v(33, 90) * mm, "end": v(15, 108) * mm});
            skLineSegment(sketch, "E87", {"start": v(15, 108) * mm, "end": v(15, 120) * mm});
            skLineSegment(sketch, "E88", {"start": v(-80, 0) * mm, "end": v(80, 0) * mm});
            skLineSegment(sketch, "E89.MirrorCS", {"start": v(-33, -90) * mm, "end": v(-15, -108) * mm});
            skLineSegment(sketch, "E90.MirrorCS", {"start": v(-15, -108) * mm, "end": v(-15, -120) * mm});
            skArc(sketch, "E91.MirrorCS", {"start": v(15, -120) * mm, "mid": v(0, -135) * mm, "end": v(-15, -120) * mm});
            skLineSegment(sketch, "E92.MirrorCS", {"start": v(15, -108) * mm, "end": v(15, -120) * mm});
            skLineSegment(sketch, "E93.MirrorCS", {"start": v(33, -90) * mm, "end": v(15, -108) * mm});
            skCircle(sketch, "E94.MirrorC", {"center": v(0, -120) * mm, "radius": 6 * mm});
            skLineSegment(sketch, "E95.MirrorCS", {"start": v(0, -90) * mm, "end": v(0, -120) * mm, "construction": true});
            skSolve(sketch);
        }
        {
            var Q0;
            {var subQ0=sQuery(id+"F16.wireOp",EDGE,"E89.MirrorCS");Q0=makeQuery(id+"F16.imprint","IMPRINT",FACE,{"disambiguationData":[TD([[makeQuery(id+"F16.imprint","IMPRINT",EDGE,{"derivedFrom":subQ0}),1.0]])]});}
            var Q1;
            Q1=makeQuery(id+"F16.imprint","IMPRINT",FACE,{"disambiguationData":[TD([[makeQuery(id+"F16.imprint","IMPRINT",EDGE,{"derivedFrom":sQuery(id+"F16.wireOp",EDGE,"E80")}),-1.0]])]});
            var Q2;
            Q2=makeQuery(id+"F16.imprint","IMPRINT",FACE,{"disambiguationData":[TD([[makeQuery(id+"F16.imprint","IMPRINT",EDGE,{"derivedFrom":makeQuery(id+"F1.opExtrude","CAP_EDGE",EDGE,{"disambiguationData":[OSD([sQuery(id+"F0.wireOp",EDGE,"E4")])],"isStart":true})}),-1.0]])]});
            var Q3;
            Q3=makeQuery(id+"F16.imprint","IMPRINT",FACE,{"disambiguationData":[TD([[makeQuery(id+"F16.imprint","IMPRINT",EDGE,{"derivedFrom":makeQuery(id+"F1.opExtrude","CAP_EDGE",EDGE,{"disambiguationData":[OSD([sQuery(id+"F0.wireOp",EDGE,"E6")])],"isStart":true})}),-1.0]])]});
            var Q4;
            Q4=makeQuery(id+"F2.opExtrude","CAP_FACE",FACE,{"disambiguationData":[OSD([sQuery(id+"F0.wireOp",EDGE,"E12"),sQuery(id+"F0.wireOp",EDGE,"E13"),sQuery(id+"F0.wireOp",EDGE,"E14"),sQuery(id+"F0.wireOp",EDGE,"E15"),sQuery(id+"F0.wireOp",EDGE,"E17.filletArc"),sQuery(id+"F0.wireOp",EDGE,"E18.filletArc"),sQuery(id+"F0.wireOp",EDGE,"E19.filletArc"),sQuery(id+"F0.wireOp",EDGE,"E20.filletArc"),sQuery(id+"F0.wireOp",EDGE,"E25.0"),sQuery(id+"F0.wireOp",EDGE,"E25.1"),sQuery(id+"F0.wireOp",EDGE,"E25.2"),sQuery(id+"F0.wireOp",EDGE,"E25.3"),sQuery(id+"F0.wireOp",EDGE,"E25.4"),sQuery(id+"F0.wireOp",EDGE,"E25.5"),sQuery(id+"F0.wireOp",EDGE,"E25.6"),sQuery(id+"F0.wireOp",EDGE,"E25.7")])],"isStart":false});
            extrude(context, id + "F17", {"entities" : qUnion([Q0, Q1, Q2, Q3]), "operationType" : NewBodyOperationType.ADD, "endBound" : BoundingType.UP_TO_SURFACE, "endBoundEntityFace" : qUnion([Q4]), "depth" : 25 * mm});
        }
    });
